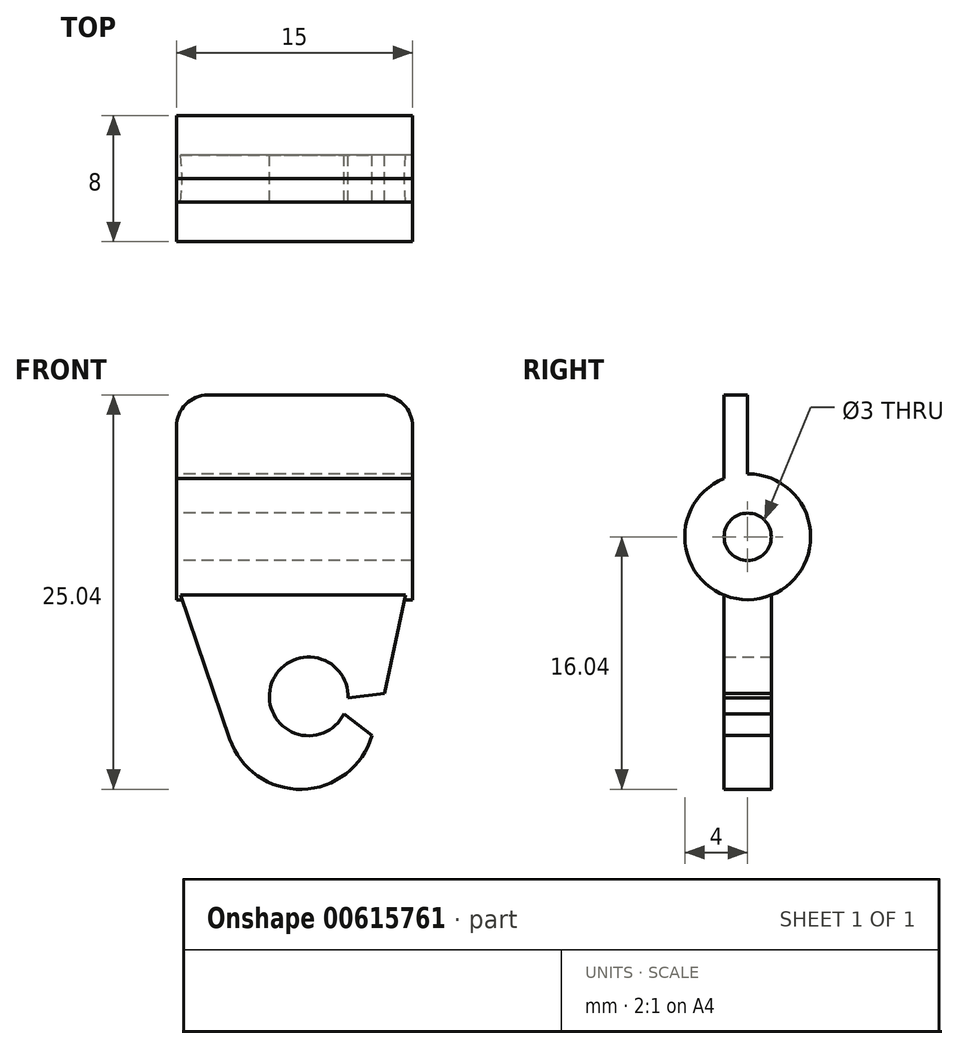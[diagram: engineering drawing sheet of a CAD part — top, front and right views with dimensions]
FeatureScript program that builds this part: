
annotation { "Feature Type Name" : "Feature", "Feature Type Description" : "" }
export const myFeature = defineFeature(function(context is Context, id is Id, definition is map)
    precondition{}
    {
        {
            var Q0;
            Q0=qCreatedBy(makeId("Right.planeOp"),FACE);
            var sketch = newSketch(context, id + "F0", { "sketchPlane" : qUnion([Q0])});
            skCircle(sketch, "E0", {"center": v(0, 0) * mm, "radius": 1.5 * mm});
            skCircle(sketch, "E1", {"center": v(0, 0) * mm, "radius": 4 * mm});
            skSolve(sketch);
        }
        {
            var Q0;
            Q0=makeQuery(id+"F0.imprint","IMPRINT",FACE,{"disambiguationData":[TD([[makeQuery(id+"F0.imprint","IMPRINT",EDGE,{"derivedFrom":sQuery(id+"F0.wireOp",EDGE,"E0")}),-1.0]])]});
            var Q1;
            Q1 = qConstructionFilter(qBodyType(qCreatedBy(id + "F0" ,EDGE), BodyType.WIRE), ConstructionObject.NO);
            extrude(context, id + "F1", {"entities" : qUnion([Q0]), "surfaceEntities" : qUnion([Q1]), "depth" : 15 * mm, "offsetDistance" : 25 * mm});
        }
        {
            var Q0;
            Q0=qCreatedBy(makeId("Front.planeOp"),FACE);
            var sketch = newSketch(context, id + "F2", { "sketchPlane" : qUnion([Q0])});
            skLineSegment(sketch, "E2", {"start": v(0, -3) * mm, "end": v(14.7, -3) * mm});
            skArc(sketch, "E3", {"start": v(10.9, -10.25) * mm, "mid": v(5.98, -9.52) * mm, "end": v(10.64, -11.25) * mm});
            skLineSegment(sketch, "E4", {"start": v(0, -3) * mm, "end": v(3.38, -12.84) * mm});
            skArc(sketch, "E5", {"start": v(3.38, -12.84) * mm, "mid": v(7.99, -16.04) * mm, "end": v(12.42, -12.61) * mm});
            skLineSegment(sketch, "E6", {"start": v(14.7, -3) * mm, "end": v(13.22, -9.94) * mm});
            skLineSegment(sketch, "E7", {"start": v(12.42, -12.61) * mm, "end": v(10.64, -11.25) * mm});
            skLineSegment(sketch, "E8", {"start": v(13.22, -9.94) * mm, "end": v(10.9, -10.25) * mm});
            skSolve(sketch);
        }
        {
            var Q0;
            Q0=makeQuery(id+"F2.imprint","IMPRINT",FACE,{"disambiguationData":[TD([[makeQuery(id+"F2.imprint","IMPRINT",EDGE,{"derivedFrom":sQuery(id+"F2.wireOp",EDGE,"E2")}),-1.0]])]});
            extrude(context, id + "F3", {"entities" : qUnion([Q0]), "operationType" : NewBodyOperationType.ADD, "endBound" : BoundingType.SYMMETRIC, "depth" : 3 * mm, "offsetDistance" : 25 * mm});
        }
        {
            var Q0;
            Q0=qCreatedBy(makeId("Front.planeOp"),FACE);
            var sketch = newSketch(context, id + "F4", { "sketchPlane" : qUnion([Q0])});
            skLineSegment(sketch, "E9.bottom", {"start": v(0, 3) * mm, "end": v(15, 3) * mm});
            skLineSegment(sketch, "E9.top", {"start": v(2, 9) * mm, "end": v(13, 9) * mm});
            skLineSegment(sketch, "E9.left", {"start": v(0, 3) * mm, "end": v(0, 7) * mm});
            skLineSegment(sketch, "E9.right", {"start": v(15, 3) * mm, "end": v(15, 7) * mm});
            skPoint(sketch, "E10.visualSharp", {"position": v(0, 9) * mm});
            skArc(sketch, "E10.filletArc", {"start": v(2, 9) * mm, "mid": v(0.59, 8.41) * mm, "end": v(0, 7) * mm});
            skPoint(sketch, "E11.visualSharp", {"position": v(15, 9) * mm});
            skArc(sketch, "E11.filletArc", {"start": v(15, 7) * mm, "mid": v(14.41, 8.41) * mm, "end": v(13, 9) * mm});
            skSolve(sketch);
        }
        {
            var Q0;
            Q0 = qSketchRegion(id + "F4", true);
            extrude(context, id + "F5", {"entities" : qUnion([Q0]), "operationType" : NewBodyOperationType.ADD, "depth" : 1.5 * mm, "offsetDistance" : 25 * mm});
        }
    });
